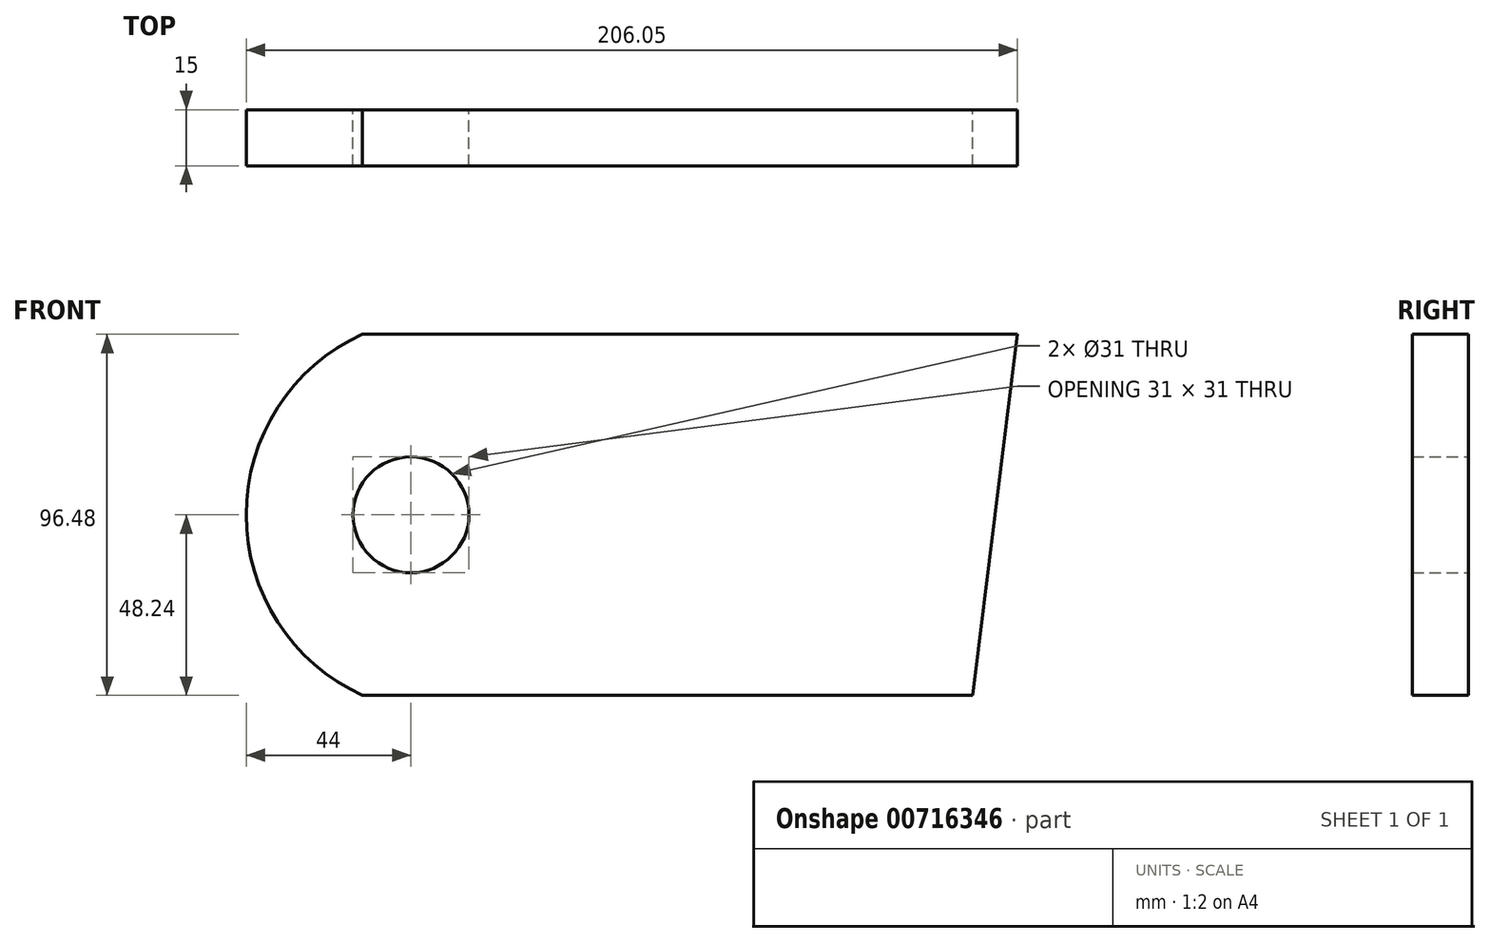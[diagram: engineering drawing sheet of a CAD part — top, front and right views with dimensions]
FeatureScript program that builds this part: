
annotation { "Feature Type Name" : "Feature", "Feature Type Description" : "" }
export const myFeature = defineFeature(function(context is Context, id is Id, definition is map)
    precondition{}
    {
        {
            var Q0;
            Q0=qCreatedBy(makeId("Front.planeOp"),FACE);
            var sketch = newSketch(context, id + "F0", { "sketchPlane" : qUnion([Q0])});
            skLineSegment(sketch, "E0.bottom", {"start": v(-65.02, -48.24) * mm, "end": v(97.98, -48.24) * mm});
            skLineSegment(sketch, "E0.top", {"start": v(-65.02, 48.24) * mm, "end": v(109.98, 48.24) * mm});
            skArc(sketch, "E1", {"start": v(-65.02, 48.24) * mm, "mid": v(-96.07, 0) * mm, "end": v(-65.02, -48.24) * mm});
            skLineSegment(sketch, "E2", {"start": v(109.98, 48.24) * mm, "end": v(97.98, -48.24) * mm});
            skPoint(sketch, "E3", {"position": v(-52.07, 0) * mm});
            skSolve(sketch);
        }
        {
            var Q0;
            Q0 = qSketchRegion(id + "F0", true);
            extrude(context, id + "F1", {"entities" : qUnion([Q0]), "depth" : 15 * mm, "offsetDistance" : 25 * mm});
        }
        {
            var Q0;
            Q0=sQuery(id+"F0.wireOp",VERTEX,"E3");
            var Q1;
            Q1=makeQuery(id+"F1.opExtrude","SWEPT_BODY",BODY,{"disambiguationData":[OSD([sQuery(id+"F0.wireOp",EDGE,"E0.bottom"),sQuery(id+"F0.wireOp",EDGE,"E0.top"),sQuery(id+"F0.wireOp",EDGE,"E1"),sQuery(id+"F0.wireOp",EDGE,"E2")])]});
            hole(context, id + "F2", {"style" : HoleStyle.SIMPLE, "endStyle" : HoleEndStyle.THROUGH, "oppositeDirection" : true, "holeDiameter" : 31 * mm, "majorDiameter" : 5 * mm, "isTappedThrough" : true, "tappedDepth" : 12 * mm, "tapClearance" : 3, "locations" : qUnion([Q0]), "scope" : qUnion([Q1])});
        }
    });
